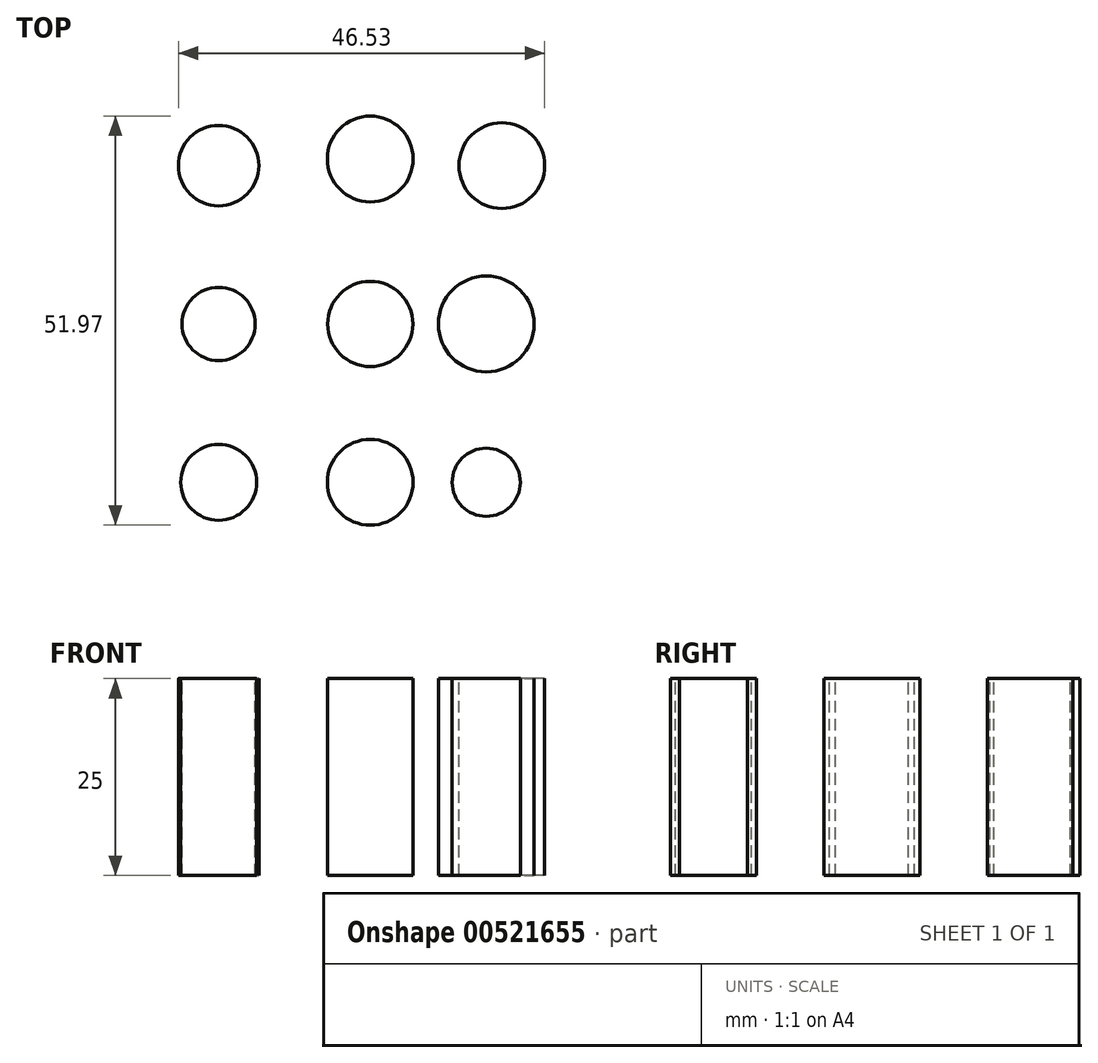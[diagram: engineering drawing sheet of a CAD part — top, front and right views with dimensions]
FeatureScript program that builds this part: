
annotation { "Feature Type Name" : "Feature", "Feature Type Description" : "" }
export const myFeature = defineFeature(function(context is Context, id is Id, definition is map)
    precondition{}
    {
        {
            var Q0;
            Q0=qCreatedBy(makeId("Top.planeOp"),FACE);
            var sketch = newSketch(context, id + "F0", { "sketchPlane" : qUnion([Q0])});
            skLineSegment(sketch, "E0.bottom", {"start": v(-30.03, -33.7) * mm, "end": v(30.03, -33.7) * mm});
            skLineSegment(sketch, "E0.top", {"start": v(-30.03, 33.7) * mm, "end": v(30.03, 33.7) * mm});
            skLineSegment(sketch, "E0.left", {"start": v(-30.03, -33.7) * mm, "end": v(-30.03, 33.7) * mm});
            skLineSegment(sketch, "E0.right", {"start": v(30.03, -33.7) * mm, "end": v(30.03, 33.7) * mm});
            skPoint(sketch, "E0.middle", {"position": v(0, 0) * mm});
            skCircle(sketch, "E1", {"center": v(-19.26, 20.11) * mm, "radius": 5.1 * mm});
            skCircle(sketch, "E2", {"center": v(0, 20.96) * mm, "radius": 5.45 * mm});
            skCircle(sketch, "E3", {"center": v(16.71, 20.11) * mm, "radius": 5.45 * mm});
            skCircle(sketch, "E4", {"center": v(14.73, -20.11) * mm, "radius": 4.33 * mm});
            skCircle(sketch, "E5", {"center": v(0, -20.11) * mm, "radius": 5.45 * mm});
            skCircle(sketch, "E6", {"center": v(-19.26, -20.11) * mm, "radius": 4.82 * mm});
            skCircle(sketch, "E7", {"center": v(-19.26, 0) * mm, "radius": 4.65 * mm});
            skCircle(sketch, "E8", {"center": v(0, 0) * mm, "radius": 5.41 * mm});
            skCircle(sketch, "E9", {"center": v(14.73, 0) * mm, "radius": 6.08 * mm});
            skSolve(sketch);
        }
        {
            var Q0;
            Q0=sQuery(id+"F0.wireOp",EDGE,"E8");
            var Q1;
            Q1=sQuery(id+"F0.wireOp",EDGE,"E1");
            var Q2;
            Q2=sQuery(id+"F0.wireOp",EDGE,"E2");
            var Q3;
            Q3=sQuery(id+"F0.wireOp",EDGE,"E7");
            var Q4;
            Q4=sQuery(id+"F0.wireOp",EDGE,"E6");
            var Q5;
            Q5=sQuery(id+"F0.wireOp",EDGE,"E5");
            var Q6;
            Q6=sQuery(id+"F0.wireOp",EDGE,"E4");
            var Q7;
            Q7=sQuery(id+"F0.wireOp",EDGE,"E9");
            var Q8;
            Q8=sQuery(id+"F0.wireOp",EDGE,"E3");
            extrude(context, id + "F1", {"bodyType" : ToolBodyType.SURFACE, "surfaceEntities" : qUnion([Q0, Q1, Q2, Q3, Q4, Q5, Q6, Q7, Q8]), "depth" : 25 * mm, "offsetDistance" : 25 * mm});
        }
    });
